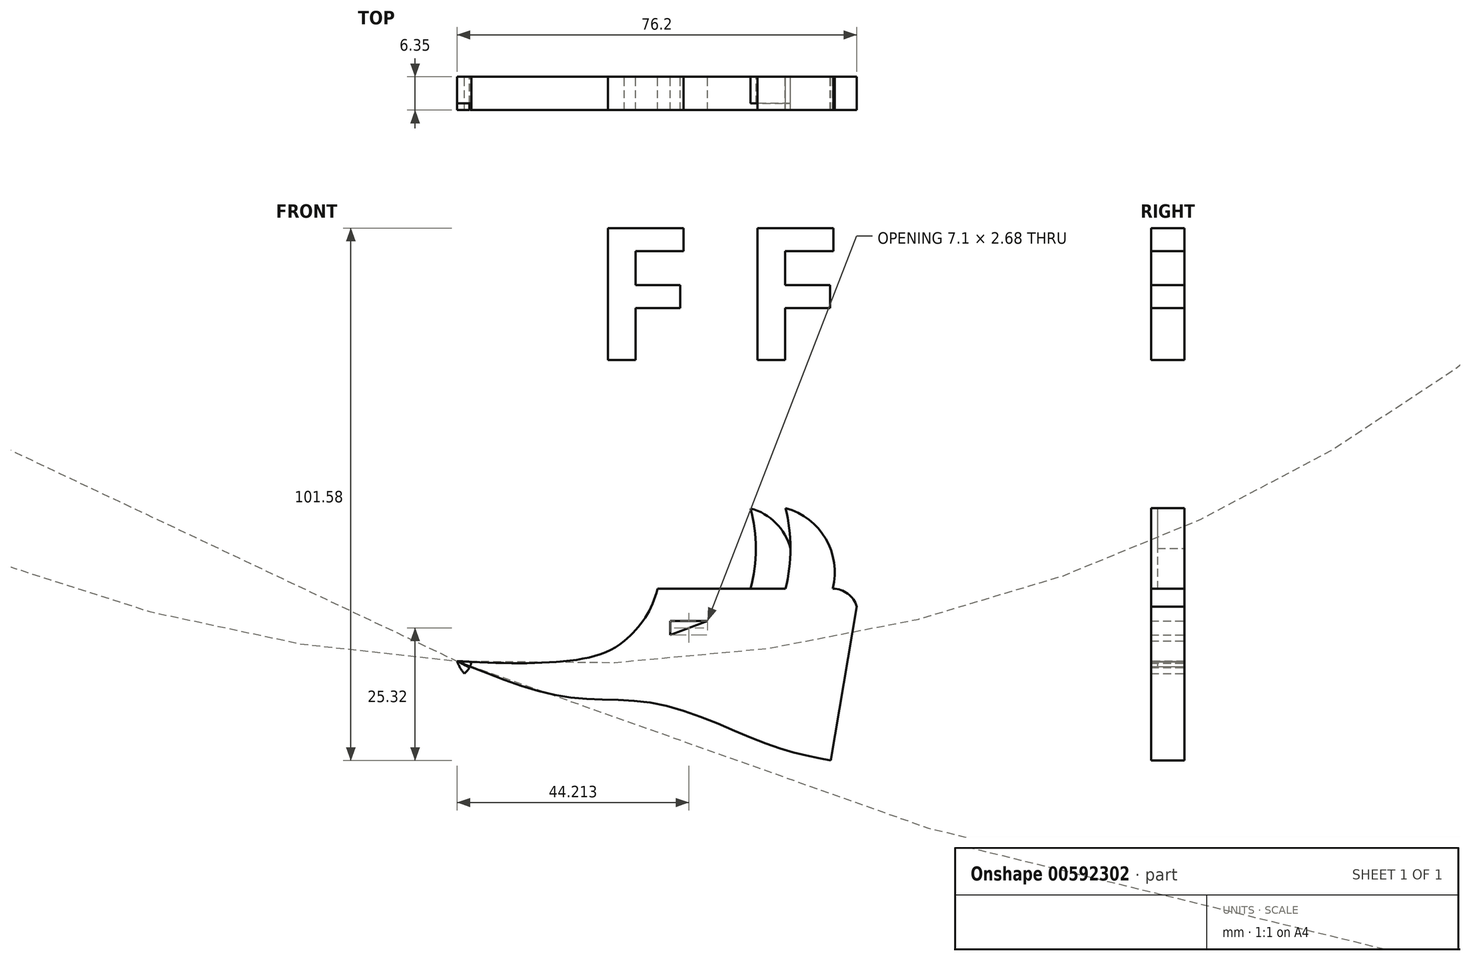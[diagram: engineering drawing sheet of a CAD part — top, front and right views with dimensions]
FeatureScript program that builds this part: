
annotation { "Feature Type Name" : "Feature", "Feature Type Description" : "" }
export const myFeature = defineFeature(function(context is Context, id is Id, definition is map)
    precondition{}
    {
        {
            var Q0;
            Q0=qCreatedBy(makeId("Front.planeOp"),FACE);
            var sketch = newSketch(context, id + "F0", { "sketchPlane" : qUnion([Q0])});
            skText(sketch, "E0", { "text": "F F", "fontName": "OpenSans-Bold.ttf"});
            skLineSegment(sketch, "E1", {"start": v(-16.11, -15.97) * mm, "end": v(17.33, -15.97) * mm});
            skArc(sketch, "E2", {"start": v(-22.48, -25.9) * mm, "mid": v(-18.46, -21.48) * mm, "end": v(-16.11, -15.97) * mm});
            skFitSpline(sketch, "E3", {"points": [v(-16.11, -15.97) * mm, v(-22.48, -25.9) * mm, v(-33.63, -29.77) * mm, v(-54.33, -29.77) * mm], "startDerivative": vector(-20.39, -34.56) * mm, "endDerivative": vector(-55.54, 3.3) * mm});
            skFitSpline(sketch, "E4", {"points": [v(-54.33, -29.77) * mm, v(-33.63, -39.86) * mm, v(-16.11, -41.45) * mm, v(4.6, -49.41) * mm, v(16.27, -52.6) * mm, v(15.74, -53.66) * mm], "startDerivative": vector(24.06, -68.96) * mm, "endDerivative": vector(-17.64, -18.46) * mm});
            skArc(sketch, "E5", {"start": v(17.33, -15.97) * mm, "mid": v(15.96, -6.44) * mm, "end": v(8.3, -0.58) * mm});
            skArc(sketch, "E6", {"start": v(8.3, -15.97) * mm, "mid": v(9.23, -8.28) * mm, "end": v(8.3, -0.58) * mm});
            skArc(sketch, "E7", {"start": v(9.23, -8.28) * mm, "mid": v(6.46, -3.43) * mm, "end": v(1.62, -0.64) * mm});
            skArc(sketch, "E8", {"start": v(1.62, -15.97) * mm, "mid": v(2.67, -8.3) * mm, "end": v(1.62, -0.64) * mm});
            skArc(sketch, "E9", {"start": v(21.87, -19.37) * mm, "mid": v(20.17, -16.92) * mm, "end": v(17.33, -15.97) * mm});
            skLineSegment(sketch, "E10", {"start": v(21.87, -19.37) * mm, "end": v(16.27, -52.6) * mm});
            skLineSegment(sketch, "E11", {"start": v(-13.67, -22.09) * mm, "end": v(-6.57, -22.09) * mm});
            skLineSegment(sketch, "E12", {"start": v(-6.57, -22.09) * mm, "end": v(-13.67, -24.77) * mm});
            skLineSegment(sketch, "E13", {"start": v(-13.67, -24.77) * mm, "end": v(-13.67, -22.09) * mm});
            skFitSpline(sketch, "E14", {"points": [v(-54.33, -29.77) * mm, v(-33.4, -36.6) * mm, v(-15.56, -38.03) * mm, v(4.8, -45.6) * mm, v(16.92, -48.75) * mm], "startDerivative": vector(78.07, -32.15) * mm, "endDerivative": vector(54.63, -10.56) * mm});
            skFitSpline(sketch, "E15", {"points": [v(-54.33, -29.77) * mm, v(-47.2, -33.23) * mm, v(-33.42, -37.03) * mm, v(-15.6, -38.68) * mm, v(4.8, -46.14) * mm, v(13.15, -48.75) * mm, v(16.8, -49.48) * mm, v(16.8, -49.43) * mm], "startDerivative": vector(47.36, -25.16) * mm, "endDerivative": vector(-1.2, 4.83) * mm});
            skArc(sketch, "E16", {"start": v(-52.96, -32.16) * mm, "mid": v(-52.05, -31.17) * mm, "end": v(-51.58, -29.92) * mm});
            const initialGuessF0  = {"E0": [-0.02873, 0.02764, 1, 0, 0.0254]};
            skSetInitialGuess(sketch, initialGuessF0);
            skSolve(sketch);
        }
        {
            var Q0;
            {var subQ1=sQuery(id+"F0.wireOp",EDGE,"E2");Q0=makeQuery(id+"F0.imprint","IMPRINT",FACE,{"disambiguationData":[TD([[makeQuery(id+"F0.imprint","IMPRINT",EDGE,{"derivedFrom":subQ1}),-1.0]])]});}
            var Q1;
            {var subQ5=sQuery(id+"F0.wireOp",EDGE,"E15");Q1=makeQuery(id+"F0.imprint","IMPRINT",FACE,{"disambiguationData":[TD([[makeQuery(id+"F0.imprint","IMPRINT",EDGE,{"derivedFrom":subQ5}),-1.0]])]});}
            var Q2;
            {var subQ0=sQuery(id+"F0.wireOp",EDGE,"E5");Q2=makeQuery(id+"F0.imprint","IMPRINT",FACE,{"disambiguationData":[TD([[makeQuery(id+"F0.imprint","IMPRINT",EDGE,{"derivedFrom":subQ0}),1.0]])]});}
            extrude(context, id + "F1", {"entities" : qUnion([Q0, Q1, Q2]), "depth" : 6.35 * mm, "offsetDistance" : 25.4 * mm});
        }
        {
            var Q0;
            {var subQ3=sQuery(id+"F0.wireOp",EDGE,"E4");var subQ5=sQuery(id+"F0.wireOp",EDGE,"E3");var subQ6=makeQuery(id+"F0.imprint","INTERSECT",VERTEX,{"derivedFrom":[subQ5,subQ3]});Q0=makeQuery(id+"F0.imprint","IMPRINT",FACE,{"disambiguationData":[TD([[makeQuery(id+"F0.imprint","IMPRINT",EDGE,{"disambiguationData":[TD([[subQ6,1.0]])],"derivedFrom":subQ5}),1.0]])]});}
            var Q1;
            {var subQ4=sQuery(id+"F0.wireOp",EDGE,"E7");Q1=makeQuery(id+"F0.imprint","IMPRINT",FACE,{"disambiguationData":[TD([[makeQuery(id+"F0.imprint","IMPRINT",EDGE,{"derivedFrom":subQ4}),1.0]])]});}
            extrude(context, id + "F2", {"entities" : qUnion([Q0, Q1]), "depth" : 5.08 * mm, "offsetDistance" : 25.4 * mm});
        }
        {
            var Q0;
            Q0=makeQuery(id+"F0.imprint","IMPRINT",FACE,{"disambiguationData":[TD([[makeQuery(id+"F0.imprint","IMPRINT",EDGE,{"derivedFrom":sQuery(id+"F0.wireOp",EDGE,"E0.sketch_text.stroke-0")}),-1.0]])]});
            var Q1;
            Q1=makeQuery(id+"F0.imprint","IMPRINT",FACE,{"disambiguationData":[TD([[makeQuery(id+"F0.imprint","IMPRINT",EDGE,{"derivedFrom":sQuery(id+"F0.wireOp",EDGE,"E0.sketch_text.stroke-10")}),-1.0]])]});
            extrude(context, id + "F3", {"entities" : qUnion([Q0, Q1]), "depth" : 6.35 * mm, "offsetDistance" : 25.4 * mm});
        }
    });
